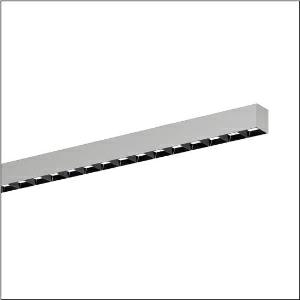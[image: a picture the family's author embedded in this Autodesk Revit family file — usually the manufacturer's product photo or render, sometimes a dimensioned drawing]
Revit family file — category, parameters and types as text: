
# Revit family: silica_r__21_51mx22dc4asb_d7c9
name_source: partatom
category: Lighting Fixtures
units: mm (PartAtom-declared; Revit-internal decimal feet)

## family parameters
Cut with Voids When Loaded = No
Host = Face
Light Source = No
Part Type = Normal
Room Calculation Point = No
Round Connector Dimension = Use Diameter
Shared = No

## types (1)
- --- (1 x LED, 10800 lm, 64.7 W, 4000K)
    Apparent Load = 65 VA
    CIE Flux Codes = 86 100 100 100 100
    Color Rendering = 80
    Color Temperature = 4000K
    Default Elevation = 1800 mm
    Description = Silica® 21, office luminaire, primary light control with darklight reflector, of PMMA, black, CAT 2 (L<= 3000cd/m²), light emission: direct distribution, primary light characteristic: symmetric, installation type: surface-mounted, LED, rated luminous flux: 10.800lm, luminous efficacy: 167lm/W, light colour: 840, colour temperature: 4000K, with terminal, 3+2-pole, max. 2.5mm², mains connection: 220..240V, AC, 50/60Hz, rated input power: 64.7W, luminaire housing, of aluminium, metallic grey (RAL 9006), length: 3.004mm, width: 53mm, height: 53mm, protection rating (complete): IP20, insulation class (complete): insulation class I (protective earthing), certification: CE, permissible operating ambient temperature: 0..+35°C, standard: EN 50419, packaging unit: 1 piece
    Height = 0 mm  [stored 0 ft]
    Lamp = 1 x LED
    Lamp Light Flux = 10800 lm
    Lamp Power = 64.7 W
    Lamp count = 1
    Length = 3004 mm
    Luminous efficacy = 167 lm/W
    Manufacturer = Siteco
    ModVariant = No
    Model = 51MX22DC4ASB
    Mounting Place = Ceiling
    Mounting Type = Recessed
    Number of Poles = 1
    OnlyDefault = Yes
    Power Factor = 1
    Product Name = Silica® 21
    Product group = office luminaire | ceiling recessed
    ProductGroupID = 401
    Protection Class = Protection class I
    Protection Degree = IP 20
    RLX_Detail_Level = 1
    RLX_Emergency_Light_Flux = 0 lm
    RLX_Emergency_Type = 0
    RLX_Emergency_Type_DB = No
    RlxData = <blob elided: 64641 chars, md5=19d080e4>
    Socket = socket
    Standby Power = 0 W
    System Light Flux = 10800 lm
    System Power = 65 W
    Type Comments = factory setting: luminous flux: 100 % | dim-lin: 254 | 366 mA
    Type Image = l_1313585.jpg
    URL = http://relux.com
    VarID = @adj_073987
    Voltage = 0 V
    Weight = 0.00 kg
    Width = 53 mm

note: [stored X ft] marks values corroborated as IEEE doubles in the binary element streams (Revit-internal decimal feet)

## geometry (parser evidence)
native form markers: Blend x4, Sweep x11
no freeform markers — native parametric forms only
